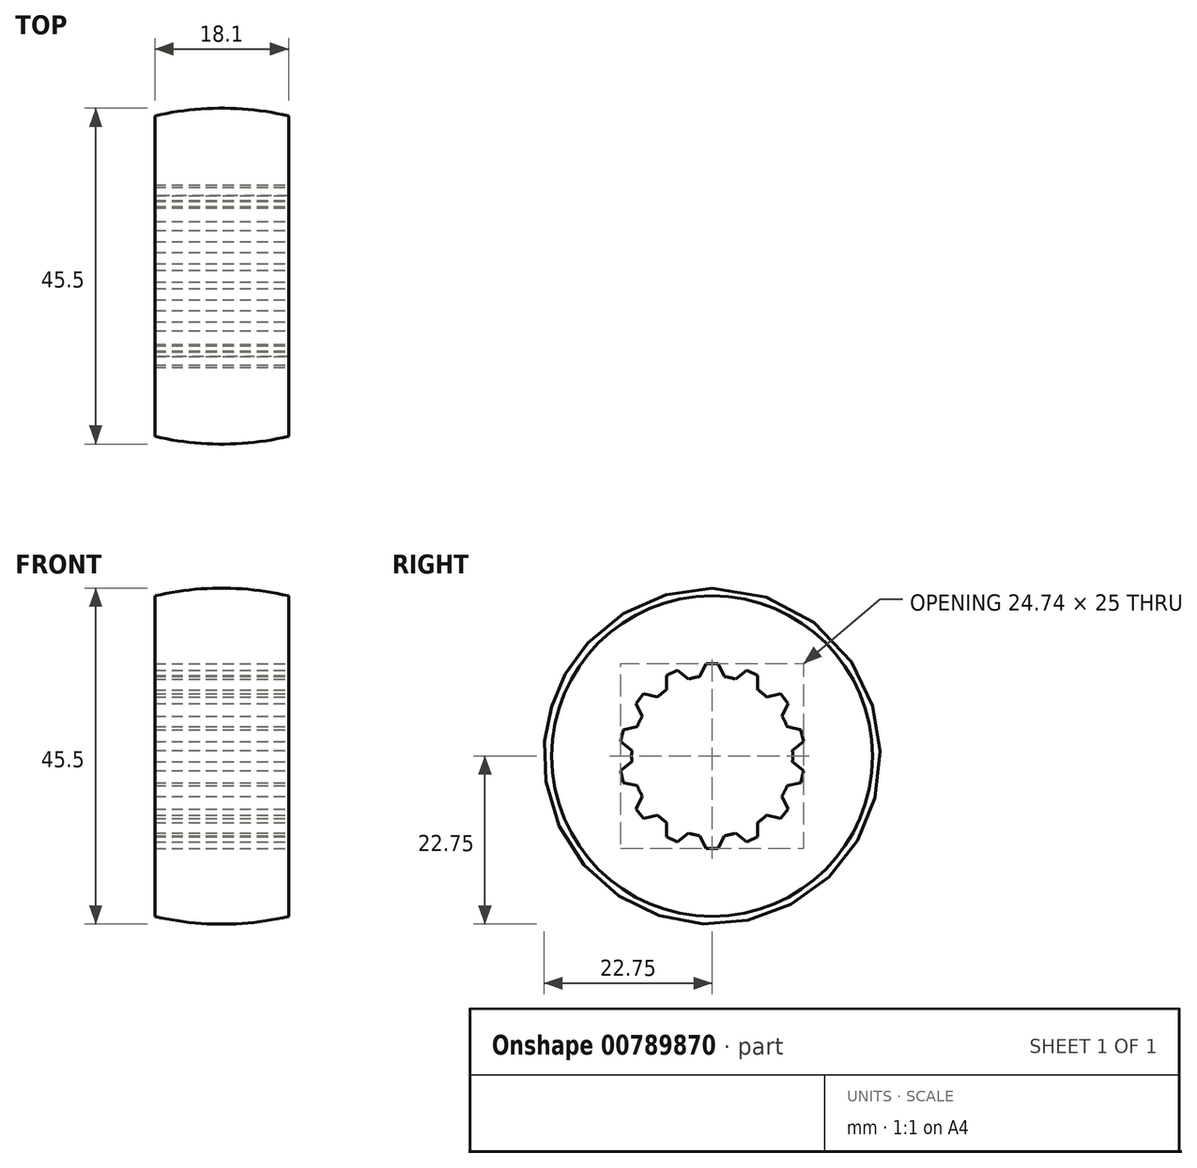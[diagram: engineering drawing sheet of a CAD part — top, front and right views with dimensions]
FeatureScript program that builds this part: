
annotation { "Feature Type Name" : "Feature", "Feature Type Description" : "" }
export const myFeature = defineFeature(function(context is Context, id is Id, definition is map)
    precondition{}
    {
        {
            var Q0;
            Q0=qCreatedBy(makeId("Front.planeOp"),FACE);
            var sketch = newSketch(context, id + "F0", { "sketchPlane" : qUnion([Q0])});
            skLineSegment(sketch, "E0", {"start": v(0, 0) * mm, "end": v(20.45, 0) * mm, "construction": true});
            skLineSegment(sketch, "E1", {"start": v(0, 10.9) * mm, "end": v(18.1, 10.9) * mm});
            skLineSegment(sketch, "E2", {"start": v(18.1, 10.9) * mm, "end": v(18.1, 21.7) * mm});
            skLineSegment(sketch, "E3", {"start": v(0, 10.9) * mm, "end": v(0, 21.7) * mm});
            skArc(sketch, "E4", {"start": v(18.1, 21.7) * mm, "mid": v(9.05, 22.75) * mm, "end": v(0, 21.7) * mm});
            skPoint(sketch, "E5", {"position": v(9.05, 22.75) * mm});
            skSolve(sketch);
        }
        {
            var Q0;
            Q0=makeQuery(id+"F0.imprint","IMPRINT",FACE,{"disambiguationData":[TD([[makeQuery(id+"F0.imprint","IMPRINT",EDGE,{"derivedFrom":sQuery(id+"F0.wireOp",EDGE,"E1")}),1.0]])]});
            var Q1;
            Q1=sQuery(id+"F0.wireOp",EDGE,"E0");
            revolve(context, id + "F1", {"surfaceOperationType" : NewSurfaceOperationType.NEW, "entities" : qUnion([Q0]), "axis" : qUnion([Q1]), "revolveType" : RevolveType.FULL});
        }
        {
            var Q0;
            Q0=makeQuery(id+"F1.opRevolve","SWEPT_FACE",FACE,{"disambiguationData":[OSD([sQuery(id+"F0.wireOp",EDGE,"E2")])]});
            var sketch = newSketch(context, id + "F2", { "sketchPlane" : qUnion([Q0])});
            skLineSegment(sketch, "E6", {"start": v(0, 0) * mm, "end": v(0, 25.69) * mm, "construction": true});
            skLineSegment(sketch, "E7", {"start": v(0.82, 12.5) * mm, "end": v(1.65, 10.77) * mm});
            skLineSegment(sketch, "E8", {"start": v(-0.82, 12.5) * mm, "end": v(-1.65, 10.77) * mm});
            skLineSegment(sketch, "E9", {"start": v(0.82, 12.5) * mm, "end": v(-0.82, 12.5) * mm});
            skLineSegment(sketch, "E10", {"start": v(1.65, 10.77) * mm, "end": v(-1.65, 10.77) * mm});
            skLineSegment(sketch, "E11.1.0", {"start": v(-4.68, 11.62) * mm, "end": v(-3.18, 10.42) * mm});
            skLineSegment(sketch, "E11.1.1", {"start": v(-4.68, 11.62) * mm, "end": v(-6.16, 10.9) * mm});
            skLineSegment(sketch, "E11.1.2", {"start": v(-6.16, 10.9) * mm, "end": v(-6.16, 8.99) * mm});
            skLineSegment(sketch, "E11.1.3", {"start": v(-3.18, 10.42) * mm, "end": v(-6.17, 8.99) * mm});
            skLineSegment(sketch, "E11.2.0", {"start": v(-9.26, 8.44) * mm, "end": v(-7.4, 8.01) * mm});
            skLineSegment(sketch, "E11.2.1", {"start": v(-9.26, 8.44) * mm, "end": v(-10.29, 7.15) * mm});
            skLineSegment(sketch, "E11.2.2", {"start": v(-10.29, 7.15) * mm, "end": v(-9.45, 5.42) * mm});
            skLineSegment(sketch, "E11.2.3", {"start": v(-7.4, 8.01) * mm, "end": v(-9.45, 5.42) * mm});
            skLineSegment(sketch, "E11.3.0", {"start": v(-12, 3.58) * mm, "end": v(-10.14, 4.01) * mm});
            skLineSegment(sketch, "E11.3.1", {"start": v(-12, 3.58) * mm, "end": v(-12.37, 1.98) * mm});
            skLineSegment(sketch, "E11.3.2", {"start": v(-12.37, 1.98) * mm, "end": v(-10.87, 0.78) * mm});
            skLineSegment(sketch, "E11.3.3", {"start": v(-10.14, 4.01) * mm, "end": v(-10.87, 0.78) * mm});
            skLineSegment(sketch, "E11.4.0", {"start": v(-12.37, -1.98) * mm, "end": v(-10.87, -0.78) * mm});
            skLineSegment(sketch, "E11.4.1", {"start": v(-12.37, -1.98) * mm, "end": v(-12, -3.58) * mm});
            skLineSegment(sketch, "E11.4.2", {"start": v(-12, -3.58) * mm, "end": v(-10.14, -4.01) * mm});
            skLineSegment(sketch, "E11.4.3", {"start": v(-10.87, -0.78) * mm, "end": v(-10.14, -4.01) * mm});
            skLineSegment(sketch, "E11.5.0", {"start": v(-10.29, -7.15) * mm, "end": v(-9.45, -5.42) * mm});
            skLineSegment(sketch, "E11.5.1", {"start": v(-10.29, -7.15) * mm, "end": v(-9.26, -8.44) * mm});
            skLineSegment(sketch, "E11.5.2", {"start": v(-9.26, -8.44) * mm, "end": v(-7.4, -8.01) * mm});
            skLineSegment(sketch, "E11.5.3", {"start": v(-9.45, -5.42) * mm, "end": v(-7.4, -8.01) * mm});
            skLineSegment(sketch, "E11.6.0", {"start": v(-6.17, -10.9) * mm, "end": v(-6.17, -8.99) * mm});
            skLineSegment(sketch, "E11.6.1", {"start": v(-6.17, -10.9) * mm, "end": v(-4.68, -11.62) * mm});
            skLineSegment(sketch, "E11.6.2", {"start": v(-4.68, -11.62) * mm, "end": v(-3.18, -10.42) * mm});
            skLineSegment(sketch, "E11.6.3", {"start": v(-6.17, -8.99) * mm, "end": v(-3.18, -10.42) * mm});
            skLineSegment(sketch, "E11.7.0", {"start": v(-0.82, -12.5) * mm, "end": v(-1.65, -10.77) * mm});
            skLineSegment(sketch, "E11.7.1", {"start": v(-0.82, -12.5) * mm, "end": v(0.82, -12.5) * mm});
            skLineSegment(sketch, "E11.7.2", {"start": v(0.82, -12.5) * mm, "end": v(1.65, -10.77) * mm});
            skLineSegment(sketch, "E11.7.3", {"start": v(-1.65, -10.77) * mm, "end": v(1.65, -10.77) * mm});
            skLineSegment(sketch, "E11.8.0", {"start": v(4.68, -11.62) * mm, "end": v(3.18, -10.42) * mm});
            skLineSegment(sketch, "E11.8.1", {"start": v(4.68, -11.62) * mm, "end": v(6.17, -10.9) * mm});
            skLineSegment(sketch, "E11.8.2", {"start": v(6.17, -10.9) * mm, "end": v(6.17, -8.99) * mm});
            skLineSegment(sketch, "E11.8.3", {"start": v(3.18, -10.42) * mm, "end": v(6.16, -8.99) * mm});
            skLineSegment(sketch, "E11.9.0", {"start": v(9.26, -8.44) * mm, "end": v(7.4, -8.01) * mm});
            skLineSegment(sketch, "E11.9.1", {"start": v(9.26, -8.44) * mm, "end": v(10.29, -7.15) * mm});
            skLineSegment(sketch, "E11.9.2", {"start": v(10.29, -7.15) * mm, "end": v(9.45, -5.42) * mm});
            skLineSegment(sketch, "E11.9.3", {"start": v(7.4, -8.01) * mm, "end": v(9.45, -5.42) * mm});
            skLineSegment(sketch, "E11.10.0", {"start": v(12, -3.58) * mm, "end": v(10.14, -4.01) * mm});
            skLineSegment(sketch, "E11.10.1", {"start": v(12, -3.58) * mm, "end": v(12.37, -1.98) * mm});
            skLineSegment(sketch, "E11.10.2", {"start": v(12.37, -1.98) * mm, "end": v(10.87, -0.78) * mm});
            skLineSegment(sketch, "E11.10.3", {"start": v(10.14, -4.01) * mm, "end": v(10.87, -0.78) * mm});
            skLineSegment(sketch, "E11.11.0", {"start": v(12.37, 1.98) * mm, "end": v(10.87, 0.78) * mm});
            skLineSegment(sketch, "E11.11.1", {"start": v(12.37, 1.98) * mm, "end": v(12, 3.58) * mm});
            skLineSegment(sketch, "E11.11.2", {"start": v(12, 3.58) * mm, "end": v(10.14, 4.01) * mm});
            skLineSegment(sketch, "E11.11.3", {"start": v(10.87, 0.78) * mm, "end": v(10.14, 4.01) * mm});
            skLineSegment(sketch, "E11.12.0", {"start": v(10.29, 7.15) * mm, "end": v(9.45, 5.42) * mm});
            skLineSegment(sketch, "E11.12.1", {"start": v(10.29, 7.15) * mm, "end": v(9.26, 8.44) * mm});
            skLineSegment(sketch, "E11.12.2", {"start": v(9.26, 8.44) * mm, "end": v(7.4, 8.01) * mm});
            skLineSegment(sketch, "E11.12.3", {"start": v(9.45, 5.42) * mm, "end": v(7.4, 8.01) * mm});
            skLineSegment(sketch, "E11.13.0", {"start": v(6.17, 10.9) * mm, "end": v(6.17, 8.99) * mm});
            skLineSegment(sketch, "E11.13.1", {"start": v(6.17, 10.9) * mm, "end": v(4.68, 11.62) * mm});
            skLineSegment(sketch, "E11.13.2", {"start": v(4.68, 11.62) * mm, "end": v(3.18, 10.42) * mm});
            skLineSegment(sketch, "E11.13.3", {"start": v(6.17, 8.99) * mm, "end": v(3.18, 10.42) * mm});
            skPoint(sketch, "E11.center", {"position": v(0, 0) * mm});
            skSolve(sketch);
        }
        {
            var Q0;
            Q0 = qSketchRegion(id + "F2", true);
            extrude(context, id + "F3", {"entities" : qUnion([Q0]), "operationType" : NewBodyOperationType.REMOVE, "endBound" : BoundingType.UP_TO_NEXT, "oppositeDirection" : true, "depth" : 25 * mm, "offsetDistance" : 25 * mm});
        }
    });
